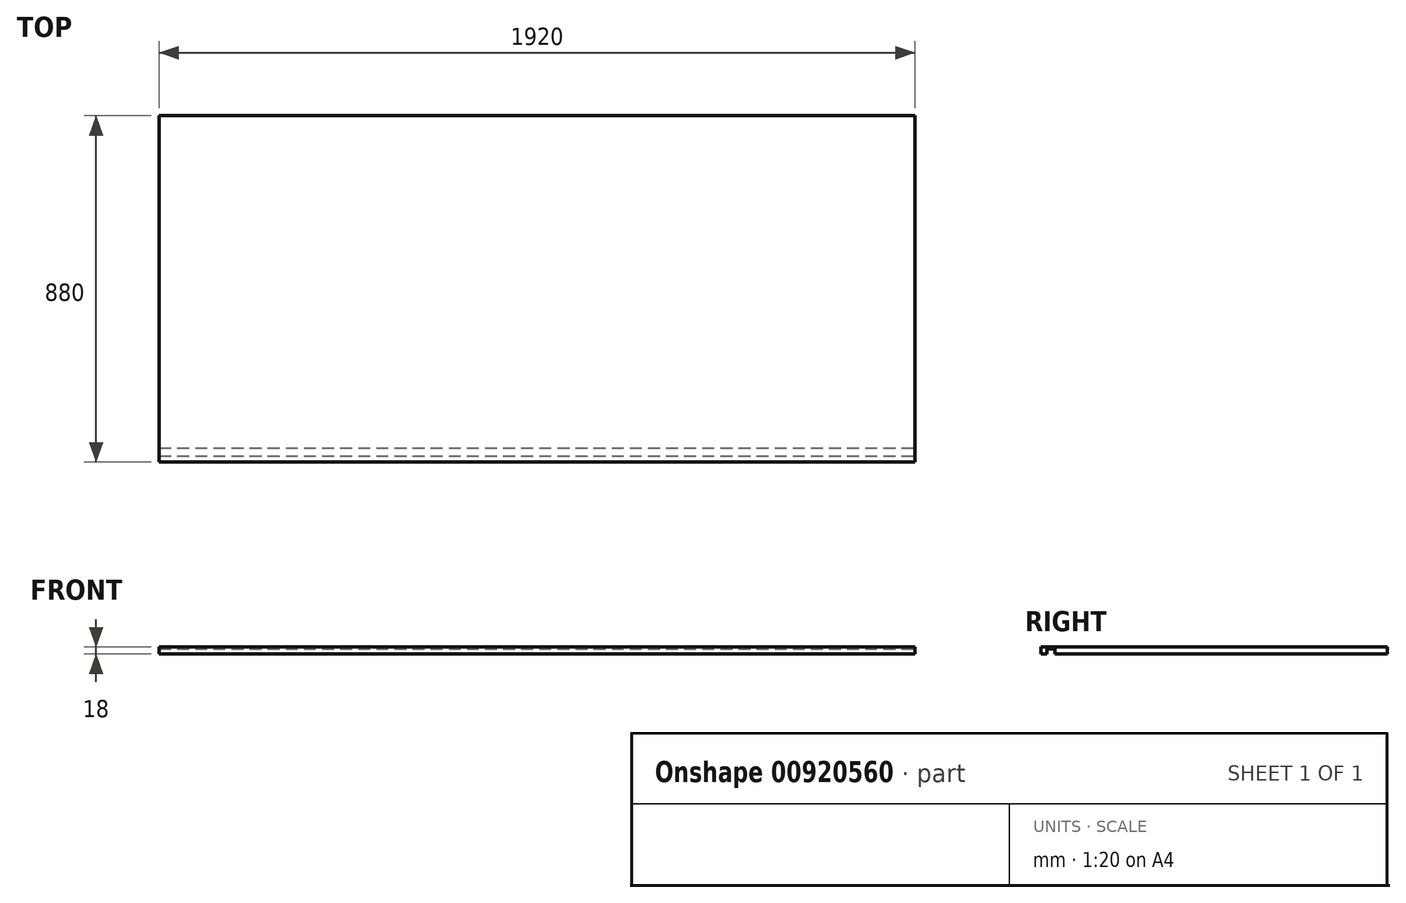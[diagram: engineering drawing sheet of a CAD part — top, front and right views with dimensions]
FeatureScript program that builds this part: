
annotation { "Feature Type Name" : "Feature", "Feature Type Description" : "" }
export const myFeature = defineFeature(function(context is Context, id is Id, definition is map)
    precondition{}
    {
        {
            var Q0;
            Q0=qCreatedBy(makeId("Top.planeOp"),FACE);
            var sketch = newSketch(context, id + "F0", { "sketchPlane" : qUnion([Q0])});
            skLineSegment(sketch, "E0.bottom", {"start": v(960, -440) * mm, "end": v(-960, -440) * mm});
            skLineSegment(sketch, "E0.top", {"start": v(960, 440) * mm, "end": v(-960, 440) * mm});
            skLineSegment(sketch, "E0.left", {"start": v(960, -440) * mm, "end": v(960, 440) * mm});
            skLineSegment(sketch, "E0.right", {"start": v(-960, -440) * mm, "end": v(-960, 440) * mm});
            skPoint(sketch, "E0.middle", {"position": v(0, 0) * mm});
            skSolve(sketch);
        }
        {
            var Q0;
            Q0=qSketchRegion(id+"F0",true);
            extrude(context, id + "F1", {"entities" : qUnion([Q0]), "depth" : 18 * mm, "offsetDistance" : 25 * mm, "symmetric" : true});
        }
        {
            var Q0;
            Q0=makeQuery(id+"F1.opExtrude","CAP_FACE",FACE,{"disambiguationData":[OSD([sQuery(id+"F0.wireOp",EDGE,"E0.bottom"),sQuery(id+"F0.wireOp",EDGE,"E0.top"),sQuery(id+"F0.wireOp",EDGE,"E0.left"),sQuery(id+"F0.wireOp",EDGE,"E0.right")])],"isStart":true});
            var sketch = newSketch(context, id + "F2", { "sketchPlane" : qUnion([Q0])});
            skLineSegment(sketch, "E1.bottom", {"start": v(-960, 424) * mm, "end": v(960, 424) * mm});
            skLineSegment(sketch, "E1.top", {"start": v(-960, 404) * mm, "end": v(960, 404) * mm});
            skLineSegment(sketch, "E1.left", {"start": v(-960, 424) * mm, "end": v(-960, 404) * mm});
            skLineSegment(sketch, "E1.right", {"start": v(960, 424) * mm, "end": v(960, 404) * mm});
            skSolve(sketch);
        }
        {
            var Q0;
            Q0 = qSketchRegion(id + "F2", true);
            extrude(context, id + "F3", {"entities" : qUnion([Q0]), "operationType" : NewBodyOperationType.REMOVE, "oppositeDirection" : true, "depth" : 13 * mm, "offsetDistance" : 25 * mm});
        }
    });
